# Revit family: Haworth_CabanaLounge_CornerSofa_EU_PRELIMINARY
name_source: partatom
category: Furniture
revit_build: Autodesk Revit 2018 (Build: 20170223_1515(x64)
units: mm (PartAtom-declared; Revit-internal decimal feet)

## family parameters
Always vertical = Yes
Cut with Voids When Loaded = No
OmniClass Number = 23.40.70.14.64.21
OmniClass Title = Systems Furniture
Room Calculation Point = No
Shared = No
Work Plane-Based = No

## types (3) — shared parameters
Assembly Code = E2020200
Description = Haworth - Cabana Lounge - Corner Sofa
Leg Offset = 7 cm
Manufacturer = Haworth
Model = SECBCF
Revision Number = 1
Screen Width = 81 cm
Seat Depth = 76 cm
Seat Height = 46 cm
Seat Width = 76 cm
Size = Verify Final Dim. w/ Haworth
URL = https://www.haworth.com
URL - Product = https://www.haworth.com
Warranty = http://www.haworth.com

## per-type parameters (varying)
| type | Actual Depth | Actual Height | Actual Width | No Screen | With Screen |
| High Screen | 81 cm | 137 cm | 81 cm | No | Yes |
| Low Screen | 81 cm | 107 cm | 81 cm | No | Yes |
| No Screen | 76 cm | 78 cm | 76 cm | Yes | No |

type visibility flags (boolean, named after types; folded from table):
- High Screen: Yes: High Screen
- Low Screen: Yes: Low Screen
- No Screen: Yes: (none)

## geometry (parser evidence)
native form markers: Sweep x13
no freeform markers — native parametric forms only
